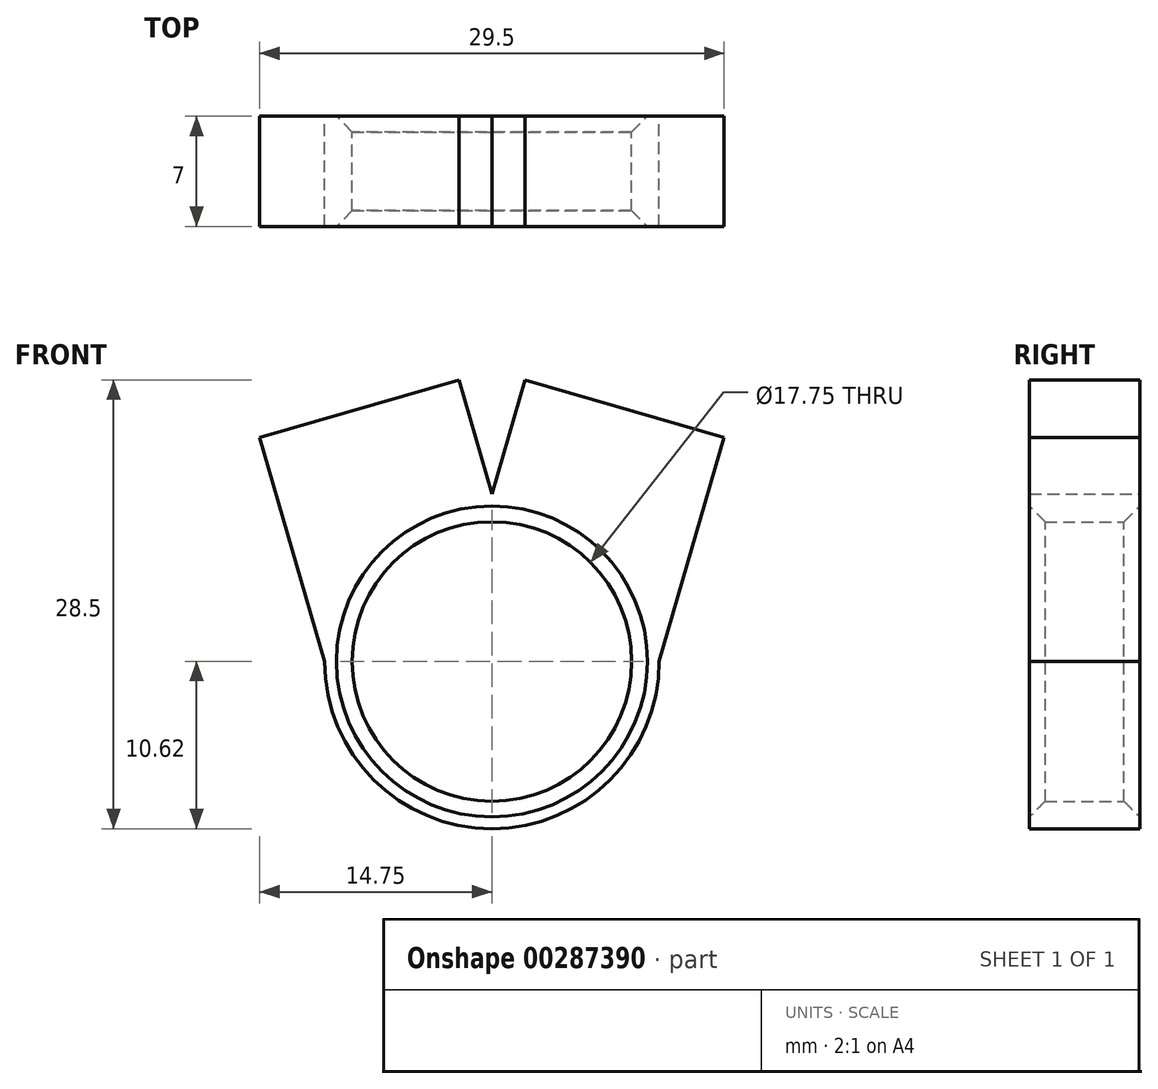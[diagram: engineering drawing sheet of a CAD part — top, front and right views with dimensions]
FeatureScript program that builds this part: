
annotation { "Feature Type Name" : "Feature", "Feature Type Description" : "" }
export const myFeature = defineFeature(function(context is Context, id is Id, definition is map)
    precondition{}
    {
        {
            var Q0;
            Q0=qCreatedBy(makeId("Front.planeOp"),FACE);
            var sketch = newSketch(context, id + "F0", { "sketchPlane" : qUnion([Q0])});
            skCircle(sketch, "E0", {"center": v(0, 0) * mm, "radius": 8.88 * mm});
            skCircle(sketch, "E1.0", {"center": v(0, 0) * mm, "radius": 10.62 * mm});
            skLineSegment(sketch, "E2", {"start": v(0, 10.62) * mm, "end": v(-2.1, 17.88) * mm});
            skLineSegment(sketch, "E3", {"start": v(-2.1, 17.88) * mm, "end": v(-14.75, 14.22) * mm});
            skLineSegment(sketch, "E4", {"start": v(-14.75, 14.22) * mm, "end": v(-10.62, 0) * mm});
            skLineSegment(sketch, "E5.MirrorCS", {"start": v(14.75, 14.22) * mm, "end": v(10.62, 0) * mm});
            skLineSegment(sketch, "E6.MirrorCS", {"start": v(2.1, 17.88) * mm, "end": v(14.75, 14.22) * mm});
            skLineSegment(sketch, "E7.MirrorCS", {"start": v(0, 10.62) * mm, "end": v(2.1, 17.88) * mm});
            skSolve(sketch);
        }
        {
            var Q0;
            {var subQ2=sQuery(id+"F0.wireOp",EDGE,"E5.MirrorCS");Q0=makeQuery(id+"F0.imprint","IMPRINT",FACE,{"disambiguationData":[TD([[makeQuery(id+"F0.imprint","IMPRINT",EDGE,{"derivedFrom":subQ2}),-1.0]])]});}
            var Q1;
            {var subQ0=sQuery(id+"F0.wireOp",EDGE,"E2");Q1=makeQuery(id+"F0.imprint","IMPRINT",FACE,{"disambiguationData":[TD([[makeQuery(id+"F0.imprint","IMPRINT",EDGE,{"derivedFrom":subQ0}),1.0]])]});}
            var Q2;
            Q2=makeQuery(id+"F0.imprint","IMPRINT",FACE,{"disambiguationData":[TD([[makeQuery(id+"F0.imprint","IMPRINT",EDGE,{"derivedFrom":sQuery(id+"F0.wireOp",EDGE,"E0")}),-1.0]])]});
            extrude(context, id + "F1", {"entities" : qUnion([Q0, Q1, Q2]), "depth" : 7 * mm});
        }
        {
            var Q0;
            Q0=makeQuery(id+"F1.opExtrude","CAP_EDGE",EDGE,{"disambiguationData":[OSD([sQuery(id+"F0.wireOp",EDGE,"E0")])],"isStart":true});
            var Q1;
            Q1=makeQuery(id+"F1.opExtrude","CAP_EDGE",EDGE,{"disambiguationData":[OSD([sQuery(id+"F0.wireOp",EDGE,"E0")])],"isStart":false});
            chamfer(context, id + "F2", {"entities" : qUnion([Q0, Q1]), "width" : 1 * mm, "tangentPropagation" : true});
        }
    });
